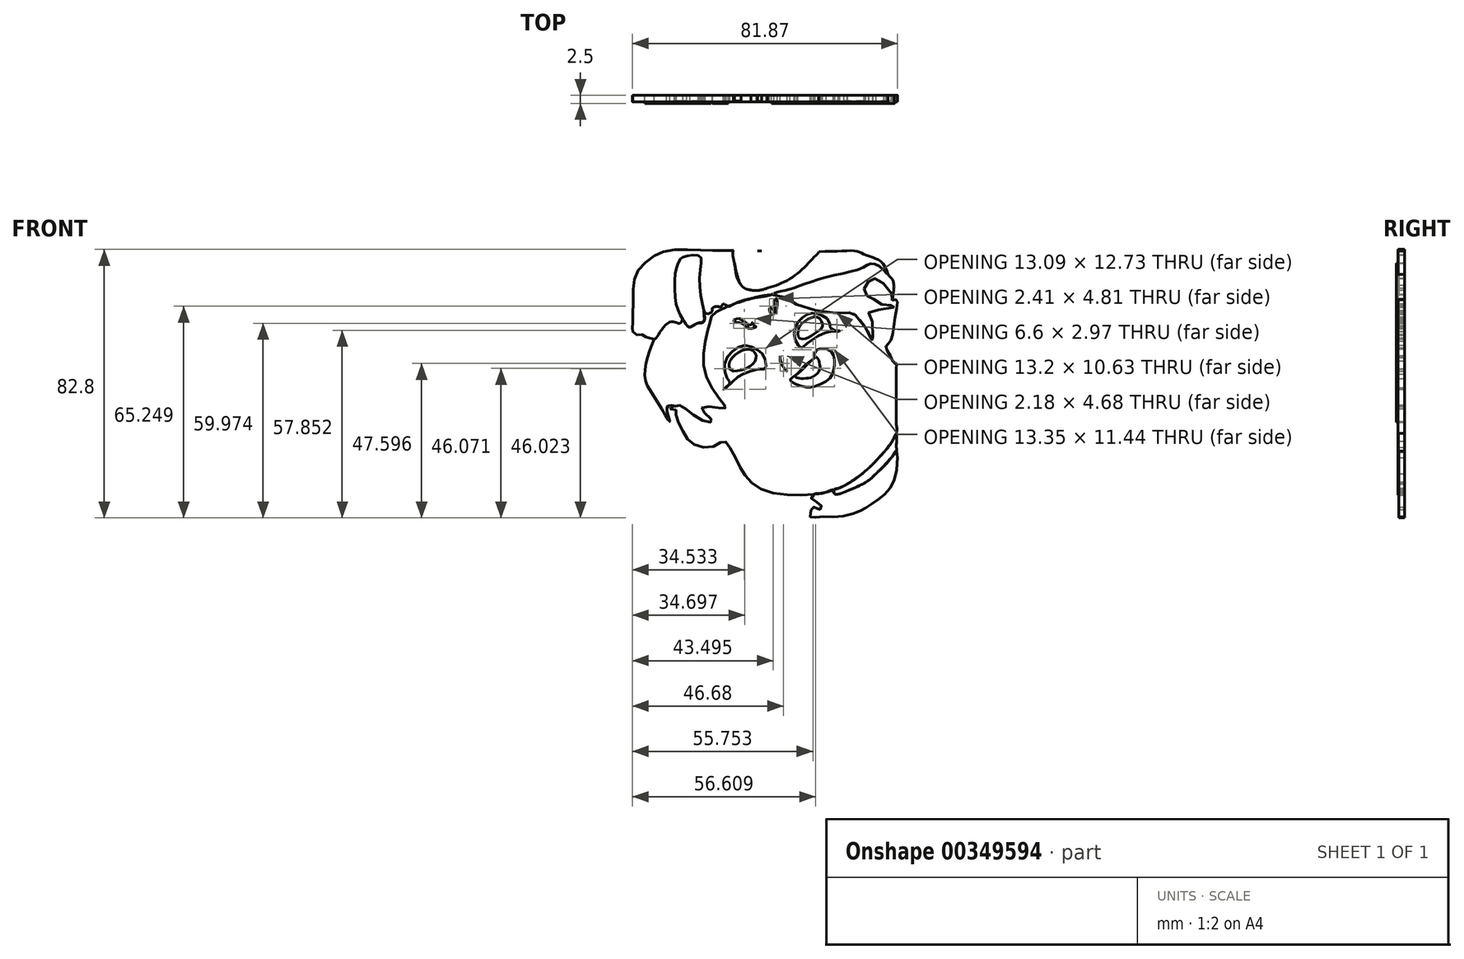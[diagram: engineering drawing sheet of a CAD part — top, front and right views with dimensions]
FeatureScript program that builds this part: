
annotation { "Feature Type Name" : "Feature", "Feature Type Description" : "" }
export const myFeature = defineFeature(function(context is Context, id is Id, definition is map)
    precondition{}
    {
        {
            var Q0;
            Q0=qCreatedBy(makeId("Front.planeOp"),FACE);
            var sketch = newSketch(context, id + "F0", { "sketchPlane" : qUnion([Q0])});
            skFitSpline(sketch, "E0", {"points": [v(-24.15, -5.47) * mm, v(-24.2, -6.05) * mm, v(-22.5, -6.32) * mm, v(-22.36, -7.7) * mm, v(-20.35, -12.88) * mm, v(-16.95, -16.94) * mm, v(-10.6, -17.54) * mm, v(-7.48, -16.05) * mm, v(-5.43, -18.57) * mm, v(-3.78, -21.62) * mm, v(-1.52, -25.87) * mm, v(4.13, -30.95) * mm, v(17.2, -32.55) * mm, v(26.11, -31.1) * mm, v(36.2, -25.08) * mm, v(45.6, -13.65) * mm, v(45.6, -11.4) * mm, v(45.6, -3.95) * mm, v(45.6, 6.64) * mm, v(45.6, 7.97) * mm, v(44.75, 8.2) * mm, v(43.96, 9.93) * mm, v(42.31, 13.07) * mm, v(43.25, 14.25) * mm, v(44.27, 16.37) * mm, v(45.6, 24.67) * mm, v(45.6, 27.62) * mm, v(44.31, 27.46) * mm, v(44.31, 28.87) * mm, v(39.9, 33.89) * mm, v(37.88, 33.82) * mm, v(35.7, 31.58) * mm, v(36.33, 29) * mm, v(38.21, 27.98) * mm, v(41.68, 26) * mm, v(44.84, 25.77) * mm, v(45.04, 25.48) * mm, v(37.22, 23.83) * mm, v(37.78, 22.4) * mm, v(38.15, 14.85) * mm, v(37.75, 15.9) * mm, v(32.4, 23.4) * mm, v(30.4, 23.46) * mm, v(15.42, 25.9) * mm, v(8.06, 29.17) * mm, v(-10.78, 23.3) * mm, v(-11.72, 21.39) * mm, v(-13.83, 12.4) * mm, v(-11.5, 0.64) * mm, v(-7.06, -5.69) * mm, v(-10.17, -5.58) * mm, v(-14.5, -6.02) * mm, v(-11.28, -9.68) * mm, v(-14.6, -9.46) * mm, v(-20.93, -5.02) * mm, v(-22.49, -5.25) * mm, v(-24.15, -5.47) * mm]});
            skFitSpline(sketch, "E1", {"points": [v(26.11, -31.1) * mm, v(26.5, -32.2) * mm, v(29.45, -31.76) * mm, v(36.2, -28.62) * mm, v(39.27, -26.07) * mm, v(45.6, -19.06) * mm, v(45.6, -18.04) * mm, v(45.6, -13.65) * mm, v(44.31, -16) * mm, v(41.68, -19.43) * mm, v(36.2, -25.08) * mm, v(30.4, -29.23) * mm, v(27.69, -30.52) * mm, v(26.11, -31.1) * mm]});
            skFitSpline(sketch, "E2", {"points": [v(20.1, -32.36) * mm, v(19.4, -33.73) * mm, v(22.14, -35.46) * mm, v(22.38, -36.71) * mm, v(21.75, -37.1) * mm, v(21.28, -36.8) * mm, v(20.26, -36.32) * mm, v(19.71, -36.48) * mm, v(19.05, -39.38) * mm, v(21.35, -39.38) * mm, v(27.4, -39.38) * mm, v(33.68, -37.81) * mm, v(36.33, -36.4) * mm, v(39.9, -34.12) * mm, v(43.1, -31.1) * mm, v(45.6, -25.57) * mm, v(45.6, -19.06) * mm, v(44.03, -21.09) * mm, v(39.27, -26.07) * mm, v(36.2, -28.62) * mm, v(29.45, -31.76) * mm, v(26.5, -32.2) * mm, v(26.11, -31.1) * mm, v(23.78, -31.76) * mm, v(21.45, -32.2) * mm, v(20.1, -32.36) * mm]});
            skFitSpline(sketch, "E3", {"points": [v(14.3, 4) * mm, v(14.98, 3.48) * mm, v(17.35, 3.35) * mm, v(19.6, 3.76) * mm, v(21.82, 5.9) * mm, v(21.79, 8.3) * mm, v(21, 9.88) * mm, v(20.06, 10.3) * mm, v(20.34, 9.92) * mm, v(17.58, 7.54) * mm, v(14.98, 4.7) * mm, v(14.3, 4) * mm]});
            skFitSpline(sketch, "E4", {"points": [v(12.77, 2.92) * mm, v(14.98, 4.7) * mm, v(19.21, 8.74) * mm, v(20.34, 9.92) * mm, v(20.06, 10.3) * mm, v(20.34, 10.87) * mm, v(20.66, 11.59) * mm, v(21.48, 12.41) * mm, v(25.05, 12.02) * mm, v(26.54, 8.92) * mm, v(26.15, 5.78) * mm, v(25.01, 3.35) * mm, v(20.7, 0.96) * mm, v(18.07, 0.6) * mm, v(14.3, 1.7) * mm, v(12.77, 2.92) * mm]});
            skFitSpline(sketch, "E5", {"points": [v(9.7, 10.29) * mm, v(10.09, 7.78) * mm, v(11.87, 5.6) * mm, v(10.22, 7.72) * mm, v(9.7, 10.29) * mm]});
            skFitSpline(sketch, "E6", {"points": [v(-5.87, 2.44) * mm, v(-6.8, 3.77) * mm, v(-7.23, 8.48) * mm, v(-4.38, 12.24) * mm, v(-0.76, 13.52) * mm, v(3.08, 11.84) * mm, v(4.8, 10.03) * mm, v(5.28, 6.46) * mm, v(3.79, 6.35) * mm, v(-1.35, 4.82) * mm, v(-4.45, 2.93) * mm, v(-7.47, 0) * mm, v(-7.75, 0) * mm, v(-7, 0.66) * mm, v(-5.78, 1.91) * mm, v(-5.87, 2.44) * mm]});
            skFitSpline(sketch, "E7", {"points": [v(-5.86, 8.45) * mm, v(-6.06, 6.94) * mm, v(-5.17, 5.75) * mm, v(-1.24, 6.24) * mm, v(1.53, 8.06) * mm, v(2.32, 9.67) * mm, v(1.96, 11.32) * mm, v(0, 12.38) * mm, v(-3.28, 11.3) * mm, v(-4.84, 9.97) * mm, v(-5.46, 9.18) * mm, v(-5.86, 8.45) * mm]});
            skFitSpline(sketch, "E8", {"points": [v(15.81, 19.62) * mm, v(15.24, 17.75) * mm, v(15.46, 15.93) * mm, v(17.4, 15.63) * mm, v(19.97, 16.97) * mm, v(22.7, 19.2) * mm, v(22.42, 21.1) * mm, v(20.9, 22.32) * mm, v(18.13, 21.46) * mm, v(15.81, 19.62) * mm]});
            skFitSpline(sketch, "E9", {"points": [v(16.26, 12.89) * mm, v(14.93, 13.9) * mm, v(14.12, 17.7) * mm, v(15.36, 20.87) * mm, v(18.24, 23.1) * mm, v(20.3, 23.54) * mm, v(23, 22.54) * mm, v(24.95, 20.73) * mm, v(25.58, 18.54) * mm, v(28.09, 17.99) * mm, v(28.13, 17.8) * mm, v(25.7, 17.9) * mm, v(21.17, 16.22) * mm, v(17.54, 13.77) * mm, v(16.54, 12.85) * mm, v(16.26, 12.89) * mm]});
            skFitSpline(sketch, "E10", {"points": [v(-4.67, 20.83) * mm, v(-2.99, 20.6) * mm, v(-1.12, 19.57) * mm, v(0.42, 18.69) * mm, v(1.54, 19.01) * mm, v(2.42, 19.2) * mm, v(1.63, 19.62) * mm, v(1.26, 20.65) * mm, v(0.46, 19.76) * mm, v(-1.12, 20.79) * mm, v(-1.87, 21.16) * mm, v(-2.52, 21.72) * mm, v(-4.25, 21.49) * mm, v(-4.67, 20.83) * mm]});
            skFitSpline(sketch, "E11", {"points": [v(7.88, 24.94) * mm, v(7.7, 24.38) * mm, v(6.67, 25.22) * mm, v(6.43, 24.15) * mm, v(7.27, 23.12) * mm, v(8.4, 24) * mm, v(8.77, 27.6) * mm, v(8.58, 28.02) * mm, v(7.97, 27.5) * mm, v(7.88, 24.94) * mm]});
            skFitSpline(sketch, "E12", {"points": [v(-4.64, 42.82) * mm, v(-4.36, 38.8) * mm, v(-2.3, 32.18) * mm, v(7.02, 31.9) * mm, v(14.3, 42.54) * mm, v(12.77, 42.72) * mm, v(8.6, 42.91) * mm, v(4.04, 42.72) * mm, v(-1.75, 42.72) * mm, v(-4.64, 42.82) * mm]});
            skFitSpline(sketch, "E13", {"points": [v(-1.75, 42.72) * mm, v(2.17, 42.61) * mm, v(4.04, 42.72) * mm, v(8.6, 42.91) * mm, v(12.77, 42.72) * mm, v(14.3, 42.54) * mm, v(21.58, 42.54) * mm, v(20.65, 41.23) * mm, v(16.91, 37.31) * mm, v(11.69, 33.49) * mm, v(5.74, 31.2) * mm, v(0.72, 30.61) * mm, v(-2.3, 32.18) * mm, v(-4.36, 38.8) * mm, v(-4.64, 42.82) * mm, v(-1.75, 42.72) * mm]});
            skFitSpline(sketch, "E14", {"points": [v(-21.8, 38.8) * mm, v(-22.59, 36.07) * mm, v(-22.47, 26.86) * mm, v(-20.59, 21.98) * mm, v(-18.15, 19.2) * mm, v(-15.6, 20.43) * mm, v(-13.83, 20.87) * mm, v(-13.83, 24.09) * mm, v(-15.15, 35.07) * mm, v(-14.93, 40.95) * mm, v(-18.81, 41.18) * mm, v(-21.03, 40.29) * mm, v(-21.8, 38.8) * mm]});
            skFitSpline(sketch, "E15", {"points": [v(-35.29, 17.41) * mm, v(-33.89, 16.62) * mm, v(-32.58, 16.94) * mm, v(-31.28, 15.68) * mm, v(-30.2, 15.82) * mm, v(-29.13, 15.45) * mm, v(-27.5, 17.36) * mm, v(-25.63, 19.79) * mm, v(-23.44, 20.87) * mm, v(-21.01, 20.43) * mm, v(-20.3, 21.47) * mm, v(-19.1, 19.75) * mm, v(-18.15, 19.2) * mm, v(-15.6, 20.43) * mm, v(-13.83, 20.87) * mm, v(-13.83, 24.09) * mm, v(-12.99, 23.3) * mm, v(-11.26, 24.09) * mm, v(-11.26, 24.87) * mm, v(-9.77, 25.57) * mm, v(-8.56, 25.39) * mm, v(-7.81, 26.27) * mm, v(-6.26, 25.6) * mm, v(-4.64, 26.23) * mm, v(0.98, 28.04) * mm, v(7.02, 29.15) * mm, v(8.6, 29.9) * mm, v(11.44, 30.56) * mm, v(15.8, 31.9) * mm, v(24.63, 34.78) * mm, v(35.12, 37.42) * mm, v(38.09, 38.8) * mm, v(41.7, 36.73) * mm, v(43, 35.43) * mm, v(41.34, 38.8) * mm, v(38.45, 40.59) * mm, v(35.68, 41.57) * mm, v(33.64, 42.54) * mm, v(26.05, 42.54) * mm, v(11.2, 42.72) * mm, v(6.93, 42.91) * mm, v(2.89, 42.65) * mm, v(0, 42.58) * mm, v(-2.32, 42.82) * mm, v(-7.23, 42.82) * mm, v(-14.72, 42.91) * mm, v(-24.36, 42.91) * mm, v(-30.16, 40.45) * mm, v(-34.65, 35.63) * mm, v(-35.57, 30.36) * mm, v(-35.64, 26.07) * mm, v(-35.7, 24.75) * mm, v(-35.7, 23.3) * mm, v(-35.7, 20.87) * mm, v(-35.84, 19.2) * mm, v(-35.84, 17.95) * mm, v(-35.29, 17.41) * mm]});
            skFitSpline(sketch, "E16", {"points": [v(-29.13, 15.45) * mm, v(-30.78, 11.07) * mm, v(-32, 3.53) * mm, v(-28.73, -2.96) * mm, v(-24.36, -9.95) * mm, v(-24.85, -8.12) * mm, v(-25.07, -5.25) * mm, v(-22.49, -5.25) * mm], "startDerivative": vector(-11.4, -27.53) * mm, "endDerivative": vector(30.69, -6.39) * mm});
            skFitSpline(sketch, "E17", {"points": [v(43, 35.43) * mm, v(44.31, 33.82) * mm, v(44.84, 31.9) * mm, v(44.31, 27.46) * mm], "startDerivative": vector(5.06, -5.41) * mm, "endDerivative": vector(-2, -11.5) * mm});
            skSolve(sketch);
        }
        {
            var Q0;
            {var subQ0=sQuery(id+"F0.wireOp",EDGE,"E17");Q0=makeQuery(id+"F0.imprint","IMPRINT",FACE,{"disambiguationData":[TD([[makeQuery(id+"F0.imprint","IMPRINT",EDGE,{"derivedFrom":subQ0}),-1.0]])]});}
            var Q1;
            {var subQ6=sQuery(id+"F0.wireOp",EDGE,"E16");Q1=makeQuery(id+"F0.imprint","IMPRINT",FACE,{"disambiguationData":[TD([[makeQuery(id+"F0.imprint","IMPRINT",EDGE,{"derivedFrom":subQ6}),1.0]])]});}
            extrude(context, id + "F1", {"entities" : qUnion([Q0, Q1]), "depth" : 2.5 * mm});
        }
        {
            var Q0;
            Q0=makeQuery(id+"F0.imprint","IMPRINT",FACE,{"disambiguationData":[TD([[makeQuery(id+"F0.imprint","IMPRINT",EDGE,{"derivedFrom":sQuery(id+"F0.wireOp",EDGE,"E5")}),-1.0]])]});
            extrude(context, id + "F2", {"entities" : qUnion([Q0]), "depth" : 2 * mm});
        }
        {
            var Q0;
            Q0=makeQuery(id+"F0.imprint","IMPRINT",FACE,{"disambiguationData":[TD([[makeQuery(id+"F0.imprint","IMPRINT",EDGE,{"derivedFrom":sQuery(id+"F0.wireOp",EDGE,"E7")}),1.0]])]});
            var Q1;
            Q1=makeQuery(id+"F0.imprint","IMPRINT",FACE,{"disambiguationData":[TD([[makeQuery(id+"F0.imprint","IMPRINT",EDGE,{"derivedFrom":sQuery(id+"F0.wireOp",EDGE,"E8")}),1.0]])]});
            var Q2;
            {var subQ0=sQuery(id+"F0.wireOp",EDGE,"E4");var subQ1=sQuery(id+"F0.wireOp",EDGE,"E3");var subQ6=makeQuery(id+"F0.imprint","INTERSECT",VERTEX,{"disambiguationData":[OD(0.0)],"derivedFrom":[subQ1,subQ0]});Q2=makeQuery(id+"F0.imprint","IMPRINT",FACE,{"disambiguationData":[TD([[makeQuery(id+"F0.imprint","IMPRINT",EDGE,{"disambiguationData":[TD([[subQ6,-1.0]])],"derivedFrom":subQ1}),1.0]])]});}
            extrude(context, id + "F3", {"entities" : qUnion([Q0, Q1, Q2]), "depth" : 2 * mm});
        }
        {
            var Q0;
            Q0=sQuery(id+"F0.wireOp",EDGE,"E5");
            extrude(context, id + "F4", {"bodyType" : ToolBodyType.SURFACE, "surfaceEntities" : qUnion([Q0]), "depth" : 2.2 * mm});
        }
        {
            var Q0;
            {var subQ0=sQuery(id+"F0.wireOp",EDGE,"E1");var subQ1=sQuery(id+"F0.wireOp",EDGE,"E0");var subQ4=makeQuery(id+"F0.imprint","INTERSECT",VERTEX,{"disambiguationData":[OD(2.0)],"derivedFrom":[subQ1,subQ0]});Q0=makeQuery(id+"F0.imprint","IMPRINT",FACE,{"disambiguationData":[TD([[makeQuery(id+"F0.imprint","IMPRINT",EDGE,{"disambiguationData":[TD([[subQ4,-1.0]])],"derivedFrom":subQ1}),-1.0]])]});}
            extrude(context, id + "F5", {"entities" : qUnion([Q0]), "depth" : 1.9 * mm});
        }
        {
            var Q0;
            {var subQ0=sQuery(id+"F0.wireOp",EDGE,"E2");var subQ9=sQuery(id+"F0.wireOp",EDGE,"E0");var subQ10=makeQuery(id+"F0.imprint","INTERSECT",VERTEX,{"disambiguationData":[OD(0.0)],"derivedFrom":[subQ9,subQ0]});Q0=makeQuery(id+"F0.imprint","IMPRINT",FACE,{"disambiguationData":[TD([[makeQuery(id+"F0.imprint","IMPRINT",EDGE,{"disambiguationData":[TD([[subQ10,-1.0]])],"derivedFrom":subQ9}),-1.0]])]});}
            extrude(context, id + "F6", {"entities" : qUnion([Q0]), "depth" : 1.7 * mm});
        }
        {
            var Q0;
            {var subQ0=sQuery(id+"F0.wireOp",EDGE,"E13");var subQ1=sQuery(id+"F0.wireOp",EDGE,"E12");var subQ14=makeQuery(id+"F0.imprint","INTERSECT",VERTEX,{"disambiguationData":[OD(6.0)],"derivedFrom":[subQ1,subQ0]});Q0=makeQuery(id+"F0.imprint","IMPRINT",FACE,{"disambiguationData":[TD([[makeQuery(id+"F0.imprint","IMPRINT",EDGE,{"disambiguationData":[TD([[subQ14,1.0]])],"derivedFrom":subQ1}),1.0]])]});}
            var Q1;
            {var subQ0=sQuery(id+"F0.wireOp",EDGE,"E15");var subQ1=sQuery(id+"F0.wireOp",EDGE,"E14");var subQ2=makeQuery(id+"F0.imprint","INTERSECT",VERTEX,{"disambiguationData":[OD(0.0)],"derivedFrom":[subQ1,subQ0]});Q1=makeQuery(id+"F0.imprint","IMPRINT",FACE,{"disambiguationData":[TD([[makeQuery(id+"F0.imprint","IMPRINT",EDGE,{"disambiguationData":[TD([[subQ2,-1.0]])],"derivedFrom":subQ1}),1.0]])]});}
            extrude(context, id + "F7", {"entities" : qUnion([Q0, Q1]), "depth" : 1.7 * mm});
        }
        {
            var Q0;
            {var subQ0=sQuery(id+"F0.wireOp",EDGE,"E13");var subQ1=sQuery(id+"F0.wireOp",EDGE,"E12");var subQ2=makeQuery(id+"F0.imprint","INTERSECT",VERTEX,{"disambiguationData":[OD(10.0)],"derivedFrom":[subQ1,subQ0]});Q0=makeQuery(id+"F0.imprint","IMPRINT",FACE,{"disambiguationData":[TD([[makeQuery(id+"F0.imprint","IMPRINT",EDGE,{"disambiguationData":[TD([[subQ2,-1.0]])],"derivedFrom":subQ1}),-1.0]])]});}
            extrude(context, id + "F8", {"entities" : qUnion([Q0]), "operationType" : NewBodyOperationType.ADD, "depth" : 1.9 * mm});
        }
        {
            var Q0;
            {var subQ0=sQuery(id+"F0.wireOp",EDGE,"E15");var subQ14=sQuery(id+"F0.wireOp",EDGE,"E0");var subQ15=makeQuery(id+"F0.imprint","INTERSECT",VERTEX,{"disambiguationData":[OD(0.0)],"derivedFrom":[subQ14,subQ0]});Q0=makeQuery(id+"F0.imprint","IMPRINT",FACE,{"disambiguationData":[TD([[makeQuery(id+"F0.imprint","IMPRINT",EDGE,{"disambiguationData":[TD([[subQ15,-1.0]])],"derivedFrom":subQ14}),-1.0]])]});}
            extrude(context, id + "F9", {"entities" : qUnion([Q0]), "depth" : 2 * mm});
        }
    });
